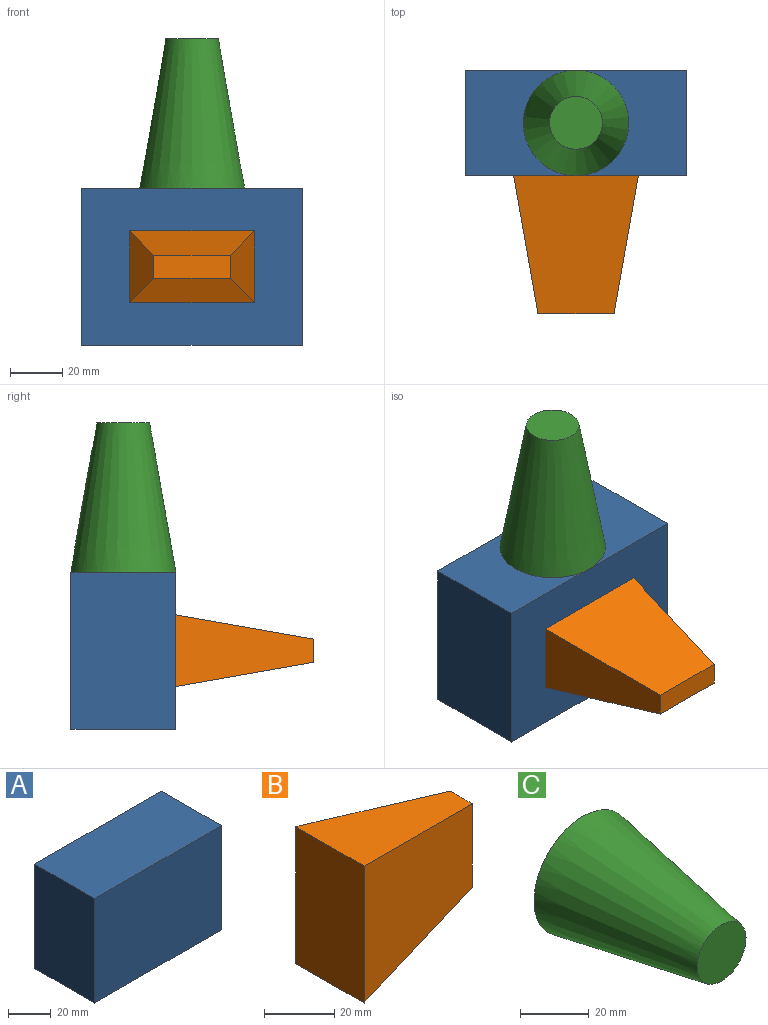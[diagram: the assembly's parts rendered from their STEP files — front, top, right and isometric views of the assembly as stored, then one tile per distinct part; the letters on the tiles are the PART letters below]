
ASSEMBLY  parts=3 mates=2
PART A: 6 faces, bbox 84.1x39.8x60 mm
  f0: plane 84.12x60mm, normal (0,-1,0), area 5047.4mm2, adj f1,f3,f4,f5
  f1: plane 60x39.79mm, normal (1,0,0), area 2387.6mm2, adj f0,f2,f4,f5
  f2: plane 84.12x60mm, normal (0,1,0), area 5047.4mm2, adj f1,f3,f4,f5
  f3: plane 60x39.79mm, normal (-1,0,0), area 2387.6mm2, adj f0,f2,f4,f5
  f4: plane 84.12x39.79mm, normal (0,0,1), area 3347.5mm2, adj f0,f1,f2,f3
  f5: plane 84.12x39.79mm, normal (0,0,-1), area 3347.5mm2, adj f0,f1,f2,f3
PART B: 6 faces, bbox 52.7x27.4x47.6 mm
  f0: plane 52.7x27.39mm, normal (0.17,0,-0.98), area 968.6mm2, adj f1,f3,f4,f5
  f1: plane 52.7x47.6mm, normal (0.17,0.98,0), area 2050mm2, adj f0,f2,f4,f5
  f2: plane 52.7x27.39mm, normal (0.17,0,0.98), area 968.6mm2, adj f1,f3,f4,f5
  f3: plane 52.7x47.6mm, normal (0.17,-0.98,0), area 2050mm2, adj f0,f2,f4,f5
  f4: plane 29.02x8.81mm, normal (1,0,0), area 255.6mm2, adj f0,f1,f2,f3
  f5: plane 47.6x27.39mm, normal (-1,0,0), area 1303.9mm2, adj f0,f1,f2,f3
PART C: 3 faces, bbox 40.2x57x40.2 mm
  f0: cone r=20.11mm half-angle=10deg, axis (0,1,0), area 5486.2mm2, adj f1,f2
  f1: plane 20.12x20.12mm, normal (0,-1,0), area 318mm2, adj f0
  f2: plane 40.22x40.22mm, normal (0,1,0), area 1270.6mm2, adj f0
PLACE A t=(-42.02,24.1,-16.7)mm fixed
PLACE B rot(axis=(0.58,-0.58,-0.58),120deg) t=(-12.02,46.26,13.3)mm
PLACE C rot(axis=(-1,0,0),90deg) t=(-42.02,24.1,43.3)mm
MATE fastened B.f5 <-> A.f0  axis (0,1,0) through (-42.02,4.2,13.3)mm
MATE fastened C.f0 <-> A.f4  axis (0,0,-1) through (-42.02,24.1,43.3)mm
